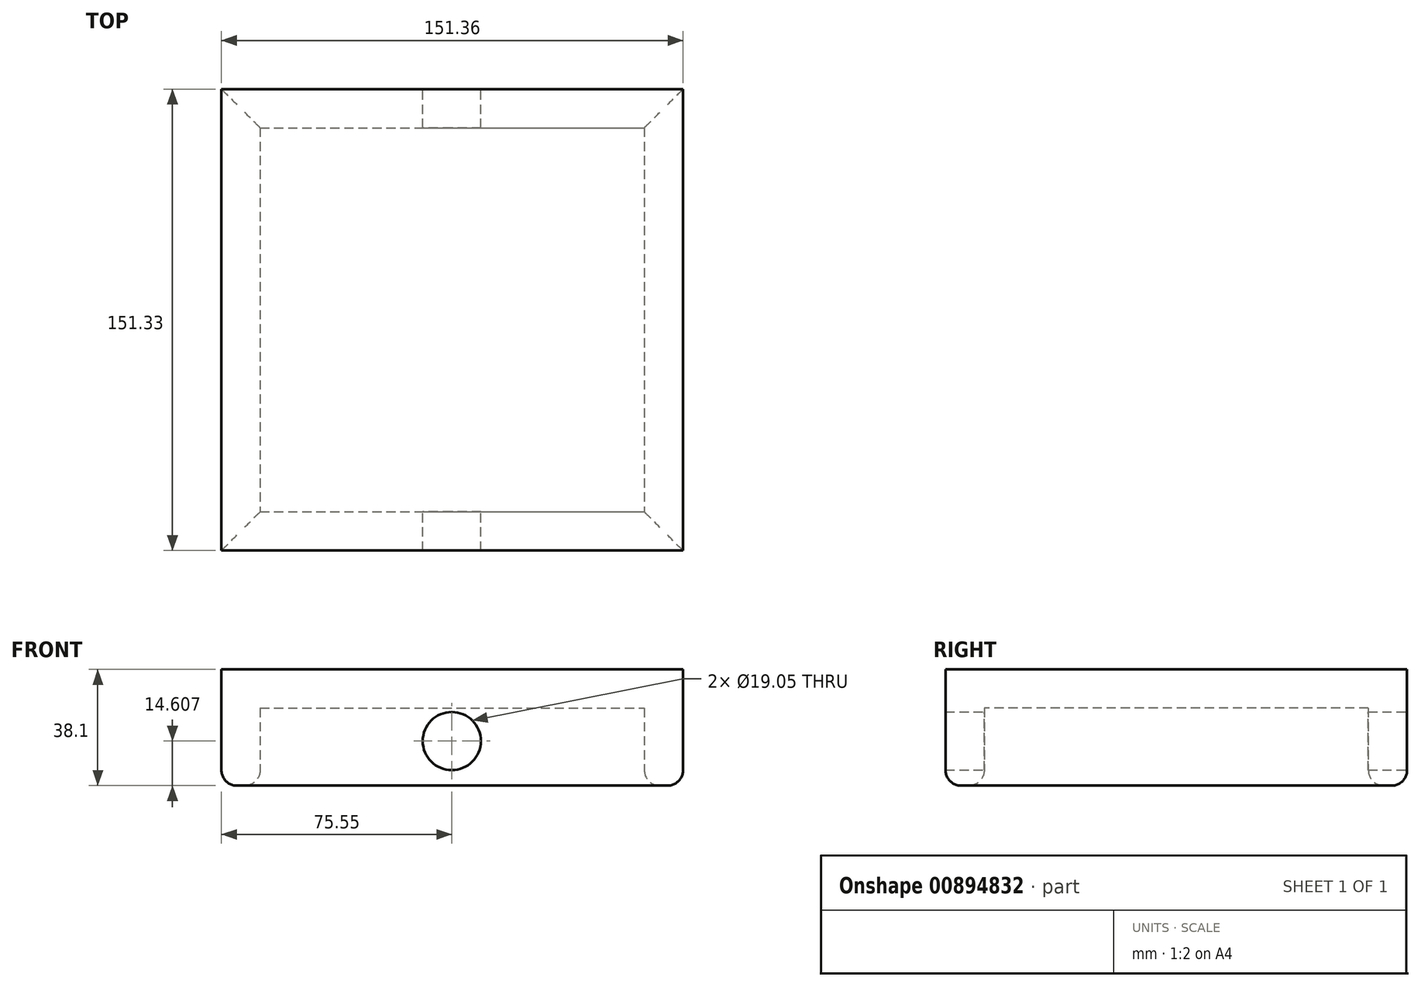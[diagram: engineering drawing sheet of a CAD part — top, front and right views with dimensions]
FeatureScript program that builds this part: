
annotation { "Feature Type Name" : "Feature", "Feature Type Description" : "" }
export const myFeature = defineFeature(function(context is Context, id is Id, definition is map)
    precondition{}
    {
        {
            var Q0;
            Q0=qCreatedBy(makeId("Top.planeOp"),FACE);
            var sketch = newSketch(context, id + "F0", { "sketchPlane" : qUnion([Q0])});
            skLineSegment(sketch, "E0.bottom", {"start": v(-75.55, 76.37) * mm, "end": v(75.81, 76.37) * mm});
            skLineSegment(sketch, "E0.top", {"start": v(-75.55, -74.96) * mm, "end": v(75.81, -74.96) * mm});
            skLineSegment(sketch, "E0.left", {"start": v(-75.55, 76.37) * mm, "end": v(-75.55, -74.96) * mm});
            skLineSegment(sketch, "E0.right", {"start": v(75.81, 76.37) * mm, "end": v(75.81, -74.96) * mm});
            skSolve(sketch);
        }
        {
            var Q0;
            Q0 = qSketchRegion(id + "F0", true);
            extrude(context, id + "F1", {"entities" : qUnion([Q0]), "depth" : 38.1 * mm, "offsetDistance" : 25.4 * mm});
        }
        {
            var Q0;
            Q0=makeQuery(id+"F1.opExtrude","CAP_FACE",FACE,{"disambiguationData":[OSD([sQuery(id+"F0.wireOp",EDGE,"E0.bottom"),sQuery(id+"F0.wireOp",EDGE,"E0.top"),sQuery(id+"F0.wireOp",EDGE,"E0.left"),sQuery(id+"F0.wireOp",EDGE,"E0.right")])],"isStart":true});
            shell(context, id + "F2", {"entities" : qUnion([Q0]), "thickness" : 12.7 * mm});
        }
        {
            var Q0;
            Q0=makeQuery(id+"F1.opExtrude","CAP_EDGE",EDGE,{"disambiguationData":[OSD([sQuery(id+"F0.wireOp",EDGE,"E0.right")])],"isStart":true});
            var Q1;
            Q1=makeQuery(id+"F1.opExtrude","CAP_EDGE",EDGE,{"disambiguationData":[OSD([sQuery(id+"F0.wireOp",EDGE,"E0.left")])],"isStart":true});
            var Q2;
            Q2=makeQuery(id+"F1.opExtrude","CAP_EDGE",EDGE,{"disambiguationData":[OSD([sQuery(id+"F0.wireOp",EDGE,"E0.top")])],"isStart":true});
            var Q3;
            {var subQ0=sQuery(id+"F0.wireOp",EDGE,"E0.left");Q3=makeQuery(id+"F2.opShell","OFFSET_EDGE",EDGE,{"disambiguationData":[OSD([subQ0]),TDD([makeQuery(id+"F1.opExtrude","CAP_EDGE",EDGE,{"disambiguationData":[OSD([subQ0])],"isStart":true})])]});}
            var Q4;
            {var subQ0=sQuery(id+"F0.wireOp",EDGE,"E0.bottom");Q4=makeQuery(id+"F2.opShell","OFFSET_EDGE",EDGE,{"disambiguationData":[OSD([subQ0]),TDD([makeQuery(id+"F1.opExtrude","CAP_EDGE",EDGE,{"disambiguationData":[OSD([subQ0])],"isStart":true})])]});}
            var Q5;
            Q5=makeQuery(id+"F1.opExtrude","CAP_EDGE",EDGE,{"disambiguationData":[OSD([sQuery(id+"F0.wireOp",EDGE,"E0.bottom")])],"isStart":true});
            var Q6;
            Q6=makeQuery(id+"F1.opExtrude","CAP_FACE",FACE,{"disambiguationData":[OSD([sQuery(id+"F0.wireOp",EDGE,"E0.bottom"),sQuery(id+"F0.wireOp",EDGE,"E0.top"),sQuery(id+"F0.wireOp",EDGE,"E0.left"),sQuery(id+"F0.wireOp",EDGE,"E0.right")])],"isStart":true});
            var Q7;
            {var subQ0=sQuery(id+"F0.wireOp",EDGE,"E0.top");Q7=makeQuery(id+"F2.opShell","OFFSET_EDGE",EDGE,{"disambiguationData":[OSD([subQ0]),TDD([makeQuery(id+"F1.opExtrude","CAP_EDGE",EDGE,{"disambiguationData":[OSD([subQ0])],"isStart":true})])]});}
            fillet(context, id + "F3", {"entities" : qUnion([Q0, Q1, Q2, Q3, Q4, Q5, Q6, Q7]), "radius" : 5.08 * mm, "tangentPropagation" : true, "allowEdgeOverflow" : false});
        }
        {
            var Q0;
            Q0=makeQuery(id+"F2.opShell","OFFSET_FACE",FACE,{"disambiguationData":[OSD([sQuery(id+"F0.wireOp",EDGE,"E0.top")])]});
            var sketch = newSketch(context, id + "F4", { "sketchPlane" : qUnion([Q0])});
            skCircle(sketch, "E1", {"center": v(0, 14.6) * mm, "radius": 9.53 * mm});
            skSolve(sketch);
        }
        {
            var Q0;
            Q0=makeQuery(id+"F4.imprint","IMPRINT",FACE,{"disambiguationData":[TD([[makeQuery(id+"F4.imprint","IMPRINT",EDGE,{"derivedFrom":sQuery(id+"F4.wireOp",EDGE,"E1")}),1.0]])]});
            extrude(context, id + "F5", {"entities" : qUnion([Q0]), "operationType" : NewBodyOperationType.REMOVE, "endBound" : BoundingType.THROUGH_ALL, "oppositeDirection" : true, "depth" : 25.4 * mm, "offsetDistance" : 25.4 * mm, "hasSecondDirection" : true, "secondDirectionBound" : SecondDirectionBoundingType.THROUGH_ALL, "secondDirectionOppositeDirection" : false, "secondDirectionDepth" : 25.4 * mm});
        }
    });
